FCSTD DOCUMENT  (FreeCAD 0.16R6705 (Git))
Label: LegMovementSim
License: All rights reserved
LicenseURL: http://en.wikipedia.org/wiki/All_rights_reserved
objects: Sketcher::SketchObject×1
note: 1 computed .brp shape members not serialized (recipe doc carries the construction recipe); baked Part::Feature solids carry a one-line shape summary decoded from their .brp

FEATURE [Sketcher::SketchObject] Sketch
  sketch-geometry (11):
    g0: LineSegment StartX=0 StartY=0 StartZ=0 EndX=219.314 EndY=-204.698 EndZ=0
    g1: LineSegment StartX=242.546 StartY=-213.933 StartZ=0 EndX=131.733 EndY=-492.716 EndZ=0
    g2: LineSegment StartX=242.546 StartY=-213.933 StartZ=0 EndX=219.314 EndY=-204.698 EndZ=0
    g3: LineSegment StartX=-8.65715 StartY=-30.8067 StartZ=0 EndX=204.539 EndY=-241.869 EndZ=0
    g4: LineSegment StartX=219.314 StartY=-204.698 StartZ=0 EndX=204.539 EndY=-241.869 EndZ=0
    g5: LineSegment StartX=0 StartY=0 StartZ=0 EndX=-27.0536 EndY=-96.271 EndZ=0
    g6: Circle [constr] CenterX=0 CenterY=0 CenterZ=0 NormalX=0 NormalY=0 NormalZ=1 Radius=40
    g7: LineSegment StartX=-29.9217 StartY=-2.16656 StartZ=0 EndX=29.9217 EndY=2.16656 EndZ=0
    g8: LineSegment StartX=29.9217 StartY=2.16656 StartZ=0 EndX=51.5873 EndY=-297.05 EndZ=0
    g9: LineSegment StartX=51.5873 StartY=-297.05 StartZ=0 EndX=-8.25606 EndY=-301.383 EndZ=0
    g10: LineSegment StartX=-8.25606 StartY=-301.383 StartZ=0 EndX=-29.9217 EndY=-2.16656 EndZ=0
  constraints (29):
    c: Coincident(g0,g-1)
    c: Distance(g-1,g0) = 300
    c: Distance(g1) = 300
    c: Coincident(g2,g1)
    c: Angle(g2,g1) = 1.5708
    c: Distance(g2) = 25
    c: Coincident(g2,g0)
    c: Distance(g3) = 300
    c: Coincident(g4,g0)
    c: Parallel(g1,g4)
    c: Distance(g4) = 40
    c: Coincident(g3,g4)
    c: Coincident(g5,g-1)
    c: PointOnObject(g3,g5)
    c: Distance(g-1,g3) = 32
    c: Distance(g-1,g5) = 100
    c: Distance(g-1,g1) = 510.022
    c: Coincident(g6,g-1)
    c: Radius(g6) = 40
    c: Coincident(g7,g8)
    c: Coincident(g8,g9)
    c: Coincident(g9,g10)
    c: Coincident(g10,g7)
    c: Angle(g7,g8) = 1.5708
    c: Equal(g10,g8)
    c: Equal(g7,g9)
    c: Distance(g9) = 60
    c: Distance(g7,g8) = 300
    c: Symmetric(g7,g7,g-1)
